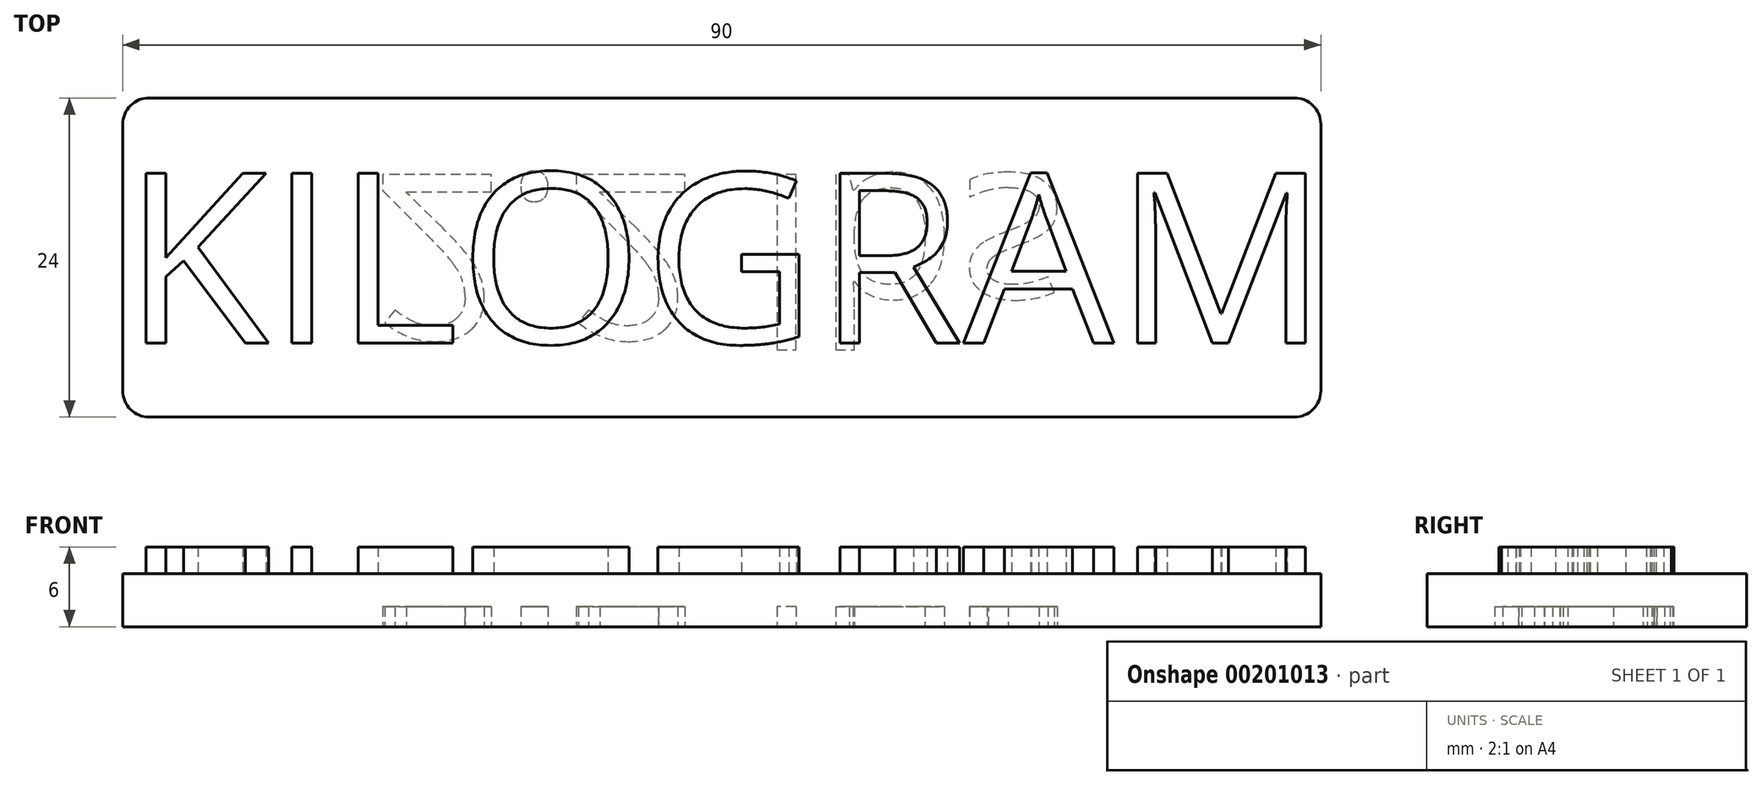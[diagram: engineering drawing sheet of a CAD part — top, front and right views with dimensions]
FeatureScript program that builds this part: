
annotation { "Feature Type Name" : "Feature", "Feature Type Description" : "" }
export const myFeature = defineFeature(function(context is Context, id is Id, definition is map)
    precondition{}
    {
        {
            var Q0;
            Q0=qCreatedBy(makeId("Top.planeOp"),FACE);
            var sketch = newSketch(context, id + "F0", { "sketchPlane" : qUnion([Q0])});
            skLineSegment(sketch, "E0.bottom", {"start": v(-45, 12) * mm, "end": v(45, 12) * mm});
            skLineSegment(sketch, "E0.top", {"start": v(-45, -12) * mm, "end": v(45, -12) * mm});
            skLineSegment(sketch, "E0.left", {"start": v(-45, 12) * mm, "end": v(-45, -12) * mm});
            skLineSegment(sketch, "E0.right", {"start": v(45, 12) * mm, "end": v(45, -12) * mm});
            skLineSegment(sketch, "E1", {"start": v(0, -12) * mm, "end": v(0, 12) * mm, "construction": true});
            skSolve(sketch);
        }
        {
            var Q0;
            Q0=makeQuery(id+"F0.imprint","IMPRINT",FACE,{"disambiguationData":[TD([[makeQuery(id+"F0.imprint","IMPRINT",EDGE,{"derivedFrom":sQuery(id+"F0.wireOp",EDGE,"E0.bottom")}),-1.0]])]});
            extrude(context, id + "F1", {"entities" : qUnion([Q0]), "depth" : 4 * mm});
        }
        {
            var Q0;
            Q0=makeQuery(id+"F1.opExtrude","SWEPT_EDGE",EDGE,{"disambiguationData":[OSD([sQuery(id+"F0.wireOp",EDGE,"E0.top"),sQuery(id+"F0.wireOp",EDGE,"E0.left")])]});
            var Q1;
            Q1=makeQuery(id+"F1.opExtrude","SWEPT_EDGE",EDGE,{"disambiguationData":[OSD([sQuery(id+"F0.wireOp",EDGE,"E0.bottom"),sQuery(id+"F0.wireOp",EDGE,"E0.right")])]});
            var Q2;
            Q2=makeQuery(id+"F1.opExtrude","SWEPT_EDGE",EDGE,{"disambiguationData":[OSD([sQuery(id+"F0.wireOp",EDGE,"E0.bottom"),sQuery(id+"F0.wireOp",EDGE,"E0.left")])]});
            var Q3;
            Q3=makeQuery(id+"F1.opExtrude","SWEPT_EDGE",EDGE,{"disambiguationData":[OSD([sQuery(id+"F0.wireOp",EDGE,"E0.top"),sQuery(id+"F0.wireOp",EDGE,"E0.right")])]});
            fillet(context, id + "F2", {"entities" : qUnion([Q0, Q1, Q2, Q3]), "radius" : 2 * mm, "tangentPropagation" : true, "allowEdgeOverflow" : false});
        }
        {
            var Q0;
            Q0=makeQuery(id+"F1.opExtrude","CAP_FACE",FACE,{"disambiguationData":[OSD([sQuery(id+"F0.wireOp",EDGE,"E0.bottom"),sQuery(id+"F0.wireOp",EDGE,"E0.top"),sQuery(id+"F0.wireOp",EDGE,"E0.left"),sQuery(id+"F0.wireOp",EDGE,"E0.right")])],"isStart":false});
            var sketch = newSketch(context, id + "F3", { "sketchPlane" : qUnion([Q0])});
            skText(sketch, "E2", { "text": "KILOGRAM", "fontName": "OpenSans-Regular.ttf"});
            const initialGuessF3  = {"E2": [-0.045, -0.00643, 1, 0, 0.01286]};
            skSetInitialGuess(sketch, initialGuessF3);
            skSolve(sketch);
        }
        {
            var Q0;
            {var subQ0=sQuery(id+"F3.wireOp",EDGE,"E2.sketch_text.stroke-4");Q0=makeQuery(id+"F3.imprint","IMPRINT",FACE,{"disambiguationData":[TD([[makeQuery(id+"F3.imprint","IMPRINT",EDGE,{"derivedFrom":subQ0}),-1.0]])]});}
            var Q1;
            {var subQ0=sQuery(id+"F3.wireOp",EDGE,"E2.sketch_text.stroke-3");var subQ1=sQuery(id+"F3.wireOp",EDGE,"E2.sketch_text.stroke-2");var subQ2=makeQuery(id+"F3.imprint","INTERSECT",VERTEX,{"derivedFrom":[subQ1,subQ0]});Q1=makeQuery(id+"F3.imprint","IMPRINT",FACE,{"disambiguationData":[TD([[makeQuery(id+"F3.imprint","IMPRINT",EDGE,{"disambiguationData":[TD([[subQ2,1.0]])],"derivedFrom":subQ1}),-1.0]])]});}
            var Q2;
            {var subQ1=sQuery(id+"F3.wireOp",EDGE,"E2.sketch_text.stroke-1");Q2=makeQuery(id+"F3.imprint","IMPRINT",FACE,{"disambiguationData":[TD([[makeQuery(id+"F3.imprint","IMPRINT",EDGE,{"derivedFrom":subQ1}),-1.0]])]});}
            var Q3;
            {var subQ0=sQuery(id+"F3.wireOp",EDGE,"E2.sketch_text.stroke-0");var subQ1=makeQuery(id+"F1.opExtrude","CAP_EDGE",EDGE,{"disambiguationData":[OSD([sQuery(id+"F0.wireOp",EDGE,"E0.top")])],"isStart":false});var subQ2=makeQuery(id+"F3.imprint","INTERSECT",VERTEX,{"derivedFrom":[subQ1,subQ0]});Q3=makeQuery(id+"F3.imprint","IMPRINT",FACE,{"disambiguationData":[TD([[makeQuery(id+"F3.imprint","IMPRINT",EDGE,{"disambiguationData":[TD([[subQ2,-1.0]])],"derivedFrom":subQ0}),-1.0]])]});}
            var Q4;
            {var subQ1=sQuery(id+"F3.wireOp",EDGE,"E2.sketch_text.stroke-8");Q4=makeQuery(id+"F3.imprint","IMPRINT",FACE,{"disambiguationData":[TD([[makeQuery(id+"F3.imprint","IMPRINT",EDGE,{"derivedFrom":subQ1}),-1.0]])]});}
            var Q5;
            {var subQ0=sQuery(id+"F3.wireOp",EDGE,"E2.sketch_text.stroke-9");var subQ1=makeQuery(id+"F1.opExtrude","CAP_EDGE",EDGE,{"disambiguationData":[OSD([sQuery(id+"F0.wireOp",EDGE,"E0.bottom")])],"isStart":false});var subQ2=makeQuery(id+"F3.imprint","INTERSECT",VERTEX,{"derivedFrom":[subQ1,subQ0]});Q5=makeQuery(id+"F3.imprint","IMPRINT",FACE,{"disambiguationData":[TD([[makeQuery(id+"F3.imprint","IMPRINT",EDGE,{"disambiguationData":[TD([[subQ2,1.0]])],"derivedFrom":subQ0}),-1.0]])]});}
            var Q6;
            {var subQ1=sQuery(id+"F3.wireOp",EDGE,"E2.sketch_text.stroke-10");Q6=makeQuery(id+"F3.imprint","IMPRINT",FACE,{"disambiguationData":[TD([[makeQuery(id+"F3.imprint","IMPRINT",EDGE,{"derivedFrom":subQ1}),-1.0]])]});}
            var Q7;
            {var subQ0=sQuery(id+"F3.wireOp",EDGE,"E2.sketch_text.stroke-11");var subQ1=makeQuery(id+"F1.opExtrude","CAP_EDGE",EDGE,{"disambiguationData":[OSD([sQuery(id+"F0.wireOp",EDGE,"E0.bottom")])],"isStart":false});var subQ2=makeQuery(id+"F3.imprint","INTERSECT",VERTEX,{"derivedFrom":[subQ1,subQ0]});Q7=makeQuery(id+"F3.imprint","IMPRINT",FACE,{"disambiguationData":[TD([[makeQuery(id+"F3.imprint","IMPRINT",EDGE,{"disambiguationData":[TD([[subQ2,-1.0]])],"derivedFrom":subQ0}),-1.0]])]});}
            var Q8;
            {var subQ0=sQuery(id+"F3.wireOp",EDGE,"E2.sketch_text.stroke-12");Q8=makeQuery(id+"F3.imprint","IMPRINT",FACE,{"disambiguationData":[TD([[makeQuery(id+"F3.imprint","IMPRINT",EDGE,{"derivedFrom":subQ0}),-1.0]])]});}
            var Q9;
            {var subQ0=sQuery(id+"F3.wireOp",EDGE,"E2.sketch_text.stroke-21");Q9=makeQuery(id+"F3.imprint","IMPRINT",FACE,{"disambiguationData":[TD([[makeQuery(id+"F3.imprint","IMPRINT",EDGE,{"derivedFrom":subQ0}),-1.0]])]});}
            var Q10;
            {var subQ0=sQuery(id+"F3.wireOp",EDGE,"E2.sketch_text.stroke-18");var subQ1=makeQuery(id+"F1.opExtrude","CAP_EDGE",EDGE,{"disambiguationData":[OSD([sQuery(id+"F0.wireOp",EDGE,"E0.top")])],"isStart":false});var subQ2=makeQuery(id+"F3.imprint","INTERSECT",VERTEX,{"derivedFrom":[subQ1,subQ0]});Q10=makeQuery(id+"F3.imprint","IMPRINT",FACE,{"disambiguationData":[TD([[makeQuery(id+"F3.imprint","IMPRINT",EDGE,{"disambiguationData":[TD([[subQ2,-1.0]])],"derivedFrom":subQ0}),-1.0]])]});}
            var Q11;
            {var subQ0=sQuery(id+"F3.wireOp",EDGE,"E2.sketch_text.stroke-19");Q11=makeQuery(id+"F3.imprint","IMPRINT",FACE,{"disambiguationData":[TD([[makeQuery(id+"F3.imprint","IMPRINT",EDGE,{"derivedFrom":subQ0}),-1.0]])]});}
            var Q12;
            {var subQ0=sQuery(id+"F3.wireOp",EDGE,"E2.sketch_text.stroke-25");Q12=makeQuery(id+"F3.imprint","IMPRINT",FACE,{"disambiguationData":[TD([[makeQuery(id+"F3.imprint","IMPRINT",EDGE,{"derivedFrom":subQ0}),-1.0]])]});}
            var Q13;
            {var subQ0=sQuery(id+"F3.wireOp",EDGE,"E2.sketch_text.stroke-22");var subQ1=makeQuery(id+"F1.opExtrude","CAP_EDGE",EDGE,{"disambiguationData":[OSD([sQuery(id+"F0.wireOp",EDGE,"E0.top")])],"isStart":false});var subQ2=makeQuery(id+"F3.imprint","INTERSECT",VERTEX,{"derivedFrom":[subQ1,subQ0]});Q13=makeQuery(id+"F3.imprint","IMPRINT",FACE,{"disambiguationData":[TD([[makeQuery(id+"F3.imprint","IMPRINT",EDGE,{"disambiguationData":[TD([[subQ2,-1.0]])],"derivedFrom":subQ0}),-1.0]])]});}
            var Q14;
            {var subQ0=sQuery(id+"F3.wireOp",EDGE,"E2.sketch_text.stroke-23");Q14=makeQuery(id+"F3.imprint","IMPRINT",FACE,{"disambiguationData":[TD([[makeQuery(id+"F3.imprint","IMPRINT",EDGE,{"derivedFrom":subQ0}),-1.0]])]});}
            var Q15;
            {var subQ5=sQuery(id+"F3.wireOp",EDGE,"E2.sketch_text.stroke-28");Q15=makeQuery(id+"F3.imprint","IMPRINT",FACE,{"disambiguationData":[TD([[makeQuery(id+"F3.imprint","IMPRINT",EDGE,{"derivedFrom":subQ5}),-1.0]])]});}
            var Q16;
            {var subQ0=sQuery(id+"F3.wireOp",EDGE,"E2.sketch_text.stroke-34");Q16=makeQuery(id+"F3.imprint","IMPRINT",FACE,{"disambiguationData":[TD([[makeQuery(id+"F3.imprint","IMPRINT",EDGE,{"derivedFrom":subQ0}),-1.0]])]});}
            var Q17;
            {var subQ0=sQuery(id+"F3.wireOp",EDGE,"E2.sketch_text.stroke-30");Q17=makeQuery(id+"F3.imprint","IMPRINT",FACE,{"disambiguationData":[TD([[makeQuery(id+"F3.imprint","IMPRINT",EDGE,{"derivedFrom":subQ0}),-1.0]])]});}
            var Q18;
            {var subQ0=sQuery(id+"F3.wireOp",EDGE,"E2.sketch_text.stroke-6");Q18=makeQuery(id+"F3.imprint","IMPRINT",FACE,{"disambiguationData":[TD([[makeQuery(id+"F3.imprint","IMPRINT",EDGE,{"derivedFrom":subQ0}),-1.0]])]});}
            var Q19;
            {var subQ0=sQuery(id+"F3.wireOp",EDGE,"E2.sketch_text.stroke-17");Q19=makeQuery(id+"F3.imprint","IMPRINT",FACE,{"disambiguationData":[TD([[makeQuery(id+"F3.imprint","IMPRINT",EDGE,{"derivedFrom":subQ0}),-1.0]])]});}
            var Q20;
            {var subQ0=sQuery(id+"F3.wireOp",EDGE,"E2.sketch_text.stroke-27");Q20=makeQuery(id+"F3.imprint","IMPRINT",FACE,{"disambiguationData":[TD([[makeQuery(id+"F3.imprint","IMPRINT",EDGE,{"derivedFrom":subQ0}),-1.0]])]});}
            var Q21;
            Q21=makeQuery(id+"F3.imprint","IMPRINT",FACE,{"disambiguationData":[TD([[makeQuery(id+"F3.imprint","IMPRINT",EDGE,{"derivedFrom":sQuery(id+"F3.wireOp",EDGE,"E2.sketch_text.stroke-45")}),-1.0]])]});
            var Q22;
            Q22=makeQuery(id+"F3.imprint","IMPRINT",FACE,{"disambiguationData":[TD([[makeQuery(id+"F3.imprint","IMPRINT",EDGE,{"derivedFrom":sQuery(id+"F3.wireOp",EDGE,"E2.sketch_text.stroke-60")}),-1.0]])]});
            var Q23;
            Q23=makeQuery(id+"F3.imprint","IMPRINT",FACE,{"disambiguationData":[TD([[makeQuery(id+"F3.imprint","IMPRINT",EDGE,{"derivedFrom":sQuery(id+"F3.wireOp",EDGE,"E2.sketch_text.stroke-76")}),-1.0]])]});
            var Q24;
            Q24=makeQuery(id+"F3.imprint","IMPRINT",FACE,{"disambiguationData":[TD([[makeQuery(id+"F3.imprint","IMPRINT",EDGE,{"derivedFrom":sQuery(id+"F3.wireOp",EDGE,"E2.sketch_text.stroke-89")}),-1.0]])]});
            extrude(context, id + "F4", {"entities" : qUnion([Q0, Q1, Q2, Q3, Q4, Q5, Q6, Q7, Q8, Q9, Q10, Q11, Q12, Q13, Q14, Q15, Q16, Q17, Q18, Q19, Q20, Q21, Q22, Q23, Q24]), "operationType" : NewBodyOperationType.ADD, "depth" : 2 * mm});
        }
        {
            var Q0;
            Q0=makeQuery(id+"F1.opExtrude","CAP_FACE",FACE,{"disambiguationData":[OSD([sQuery(id+"F0.wireOp",EDGE,"E0.bottom"),sQuery(id+"F0.wireOp",EDGE,"E0.top"),sQuery(id+"F0.wireOp",EDGE,"E0.left"),sQuery(id+"F0.wireOp",EDGE,"E0.right")])],"isStart":true});
            var sketch = newSketch(context, id + "F5", { "sketchPlane" : qUnion([Q0])});
            skText(sketch, "E3", { "text": "2.2 lbs", "fontName": "OpenSans-Regular.ttf"});
            const initialGuessF5  = {"E3": [-0.02631, -0.00625, 1, 0, 0.0125]};
            skSetInitialGuess(sketch, initialGuessF5);
            skSolve(sketch);
        }
        {
            var Q0;
            Q0=makeQuery(id+"F5.imprint","IMPRINT",FACE,{"disambiguationData":[TD([[makeQuery(id+"F5.imprint","IMPRINT",EDGE,{"derivedFrom":sQuery(id+"F5.wireOp",EDGE,"E3.sketch_text.stroke-86")}),-1.0]])]});
            var Q1;
            Q1=makeQuery(id+"F5.imprint","IMPRINT",FACE,{"disambiguationData":[TD([[makeQuery(id+"F5.imprint","IMPRINT",EDGE,{"derivedFrom":sQuery(id+"F5.wireOp",EDGE,"E3.sketch_text.stroke-70")}),-1.0]])]});
            var Q2;
            Q2=makeQuery(id+"F5.imprint","IMPRINT",FACE,{"disambiguationData":[TD([[makeQuery(id+"F5.imprint","IMPRINT",EDGE,{"derivedFrom":sQuery(id+"F5.wireOp",EDGE,"E3.sketch_text.stroke-39")}),-1.0]])]});
            var Q3;
            Q3=makeQuery(id+"F5.imprint","IMPRINT",FACE,{"disambiguationData":[TD([[makeQuery(id+"F5.imprint","IMPRINT",EDGE,{"derivedFrom":sQuery(id+"F5.wireOp",EDGE,"E3.sketch_text.stroke-19")}),-1.0]])]});
            var Q4;
            Q4=makeQuery(id+"F5.imprint","IMPRINT",FACE,{"disambiguationData":[TD([[makeQuery(id+"F5.imprint","IMPRINT",EDGE,{"derivedFrom":sQuery(id+"F5.wireOp",EDGE,"E3.sketch_text.stroke-0")}),-1.0]])]});
            var Q5;
            Q5=makeQuery(id+"F5.imprint","IMPRINT",FACE,{"disambiguationData":[TD([[makeQuery(id+"F5.imprint","IMPRINT",EDGE,{"derivedFrom":sQuery(id+"F5.wireOp",EDGE,"E3.sketch_text.stroke-51")}),-1.0]])]});
            var Q6;
            Q6=makeQuery(id+"F5.imprint","IMPRINT",FACE,{"disambiguationData":[TD([[makeQuery(id+"F5.imprint","IMPRINT",EDGE,{"derivedFrom":sQuery(id+"F5.wireOp",EDGE,"E3.sketch_text.stroke-20")}),-1.0]])]});
            extrude(context, id + "F6", {"entities" : qUnion([Q0, Q1, Q2, Q3, Q4, Q5, Q6]), "operationType" : NewBodyOperationType.REMOVE, "oppositeDirection" : true, "depth" : 1.5 * mm});
        }
    });
